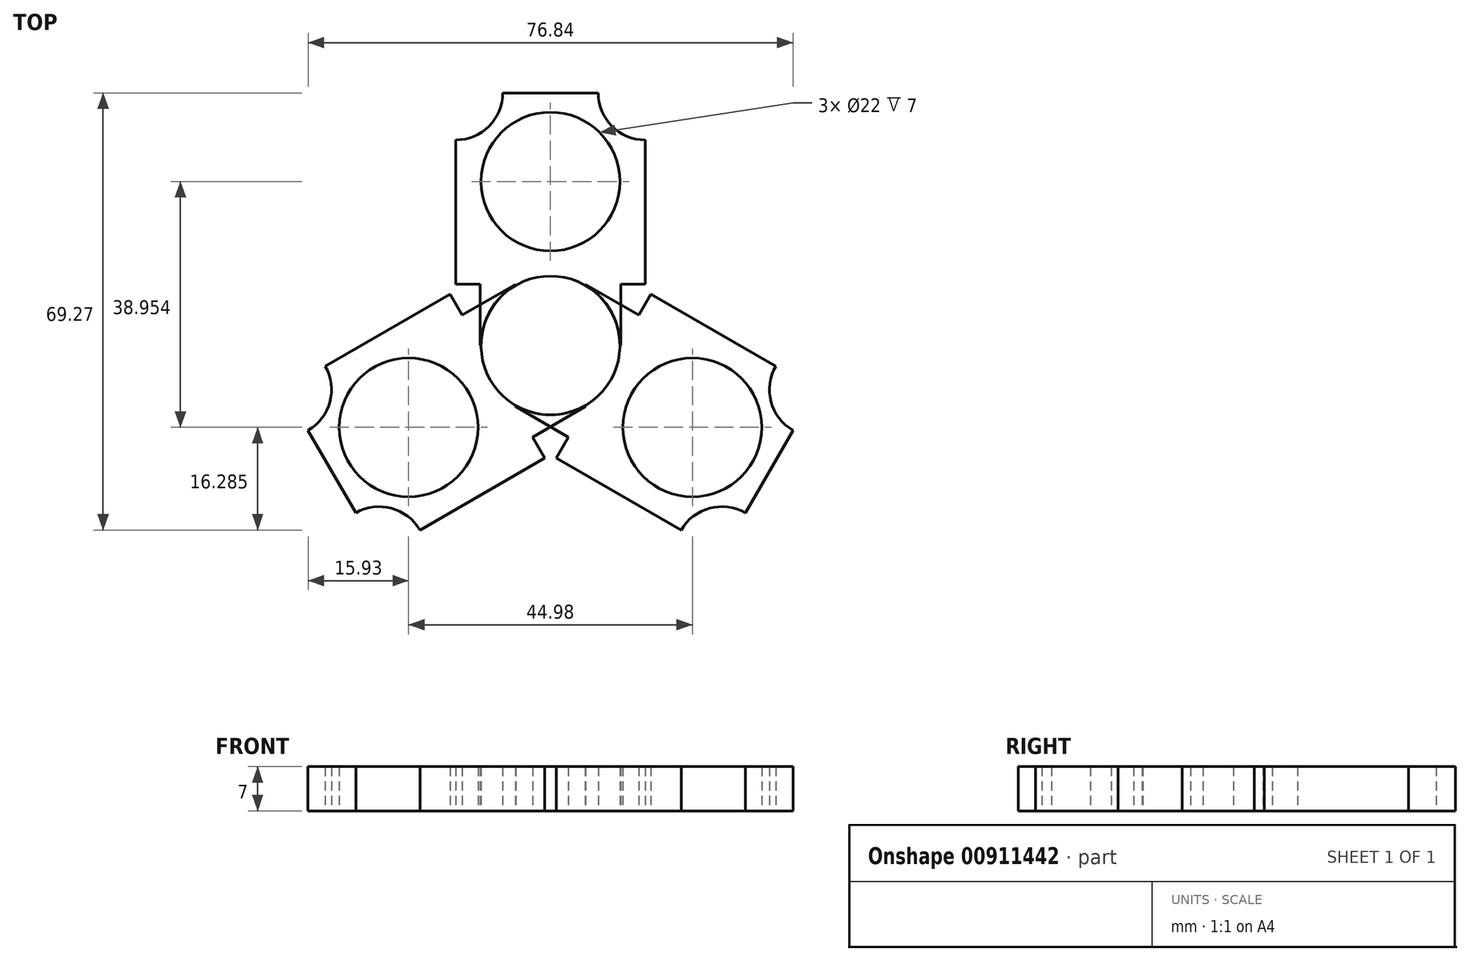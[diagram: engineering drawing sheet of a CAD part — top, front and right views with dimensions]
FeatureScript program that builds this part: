
annotation { "Feature Type Name" : "Feature", "Feature Type Description" : "" }
export const myFeature = defineFeature(function(context is Context, id is Id, definition is map)
    precondition{}
    {
        {
            var Q0;
            Q0=qCreatedBy(makeId("Top.planeOp"),FACE);
            var sketch = newSketch(context, id + "F0", { "sketchPlane" : qUnion([Q0])});
            skCircle(sketch, "E0", {"center": v(0, 0) * mm, "radius": 11 * mm});
            skLineSegment(sketch, "E1.bottom", {"start": v(0, 0) * mm, "end": v(15, 0) * mm});
            skLineSegment(sketch, "E1.top", {"start": v(0, 40) * mm, "end": v(15, 40) * mm});
            skLineSegment(sketch, "E1.left", {"start": v(0, 0) * mm, "end": v(0, 40) * mm});
            skLineSegment(sketch, "E1.right", {"start": v(15, 0) * mm, "end": v(15, 40) * mm});
            skLineSegment(sketch, "E2.bottom", {"start": v(0, 0) * mm, "end": v(-15, 0) * mm});
            skLineSegment(sketch, "E2.top", {"start": v(0, 40) * mm, "end": v(-15, 40) * mm});
            skLineSegment(sketch, "E2.right", {"start": v(-15, 0) * mm, "end": v(-15, 40) * mm});
            skLineSegment(sketch, "E3", {"start": v(0, 40) * mm, "end": v(0, 25.97) * mm});
            skCircle(sketch, "E4", {"center": v(0, 25.97) * mm, "radius": 11 * mm});
            skCircle(sketch, "E5", {"center": v(15, 40) * mm, "radius": 7.44 * mm});
            skCircle(sketch, "E6", {"center": v(-15, 40) * mm, "radius": 7.44 * mm});
            skLineSegment(sketch, "E7.bottom", {"start": v(-15, 0) * mm, "end": v(-11.16, 0) * mm});
            skLineSegment(sketch, "E7.top", {"start": v(-15, 9.7) * mm, "end": v(-11.16, 9.7) * mm});
            skLineSegment(sketch, "E7.left", {"start": v(-15, 0) * mm, "end": v(-15, 9.7) * mm});
            skLineSegment(sketch, "E7.right", {"start": v(-11.16, 0) * mm, "end": v(-11.16, 9.7) * mm});
            skLineSegment(sketch, "E8.bottom", {"start": v(15, 0) * mm, "end": v(11.16, 0) * mm});
            skLineSegment(sketch, "E8.top", {"start": v(15, 9.7) * mm, "end": v(11.16, 9.7) * mm});
            skLineSegment(sketch, "E8.left", {"start": v(15, 0) * mm, "end": v(15, 9.7) * mm});
            skLineSegment(sketch, "E8.right", {"start": v(11.16, 0) * mm, "end": v(11.16, 9.7) * mm});
            skSolve(sketch);
        }
        {
            var Q0;
            {var subQ1=sQuery(id+"F0.wireOp",EDGE,"E1.bottom");var subQ10=sQuery(id+"F0.wireOp",EDGE,"E0");var subQ11=makeQuery(id+"F0.imprint","INTERSECT",VERTEX,{"derivedFrom":[subQ10,subQ1]});Q0=makeQuery(id+"F0.imprint","IMPRINT",FACE,{"disambiguationData":[TD([[makeQuery(id+"F0.imprint","IMPRINT",EDGE,{"disambiguationData":[TD([[subQ11,-1.0]])],"derivedFrom":subQ10}),-1.0]])]});}
            var Q1;
            {var subQ1=sQuery(id+"F0.wireOp",EDGE,"E0");var subQ10=sQuery(id+"F0.wireOp",EDGE,"E2.bottom");var subQ12=makeQuery(id+"F0.imprint","INTERSECT",VERTEX,{"derivedFrom":[subQ1,subQ10]});Q1=makeQuery(id+"F0.imprint","IMPRINT",FACE,{"disambiguationData":[TD([[makeQuery(id+"F0.imprint","IMPRINT",EDGE,{"disambiguationData":[TD([[subQ12,1.0]])],"derivedFrom":subQ1}),-1.0]])]});}
            extrude(context, id + "F1", {"entities" : qUnion([Q0, Q1]), "depth" : 7 * mm, "offsetDistance" : 25 * mm});
        }
        {
            var Q0;
            Q0=qCreatedBy(makeId("Front.planeOp"),FACE);
            var sketch = newSketch(context, id + "F2", { "sketchPlane" : qUnion([Q0])});
            skLineSegment(sketch, "E9", {"start": v(0, 0) * mm, "end": v(0, 33.84) * mm});
            skSolve(sketch);
        }
        {
            var Q0;
            Q0=makeQuery(id+"F1.opExtrude","SWEPT_BODY",BODY,{"disambiguationData":[OSD([sQuery(id+"F0.wireOp",EDGE,"E0"),sQuery(id+"F0.wireOp",EDGE,"E1.bottom"),sQuery(id+"F0.wireOp",EDGE,"E1.top"),sQuery(id+"F0.wireOp",EDGE,"E1.right"),sQuery(id+"F0.wireOp",EDGE,"E2.bottom"),sQuery(id+"F0.wireOp",EDGE,"E2.top"),sQuery(id+"F0.wireOp",EDGE,"E2.right"),sQuery(id+"F0.wireOp",EDGE,"E4")])]});
            var Q1;
            Q1=sQuery(id+"F2.wireOp",EDGE,"E9");
            transform(context, id + "F3", {"entities" : qUnion([Q0]), "transformType" : TransformType.ROTATION, "transformAxis" : qUnion([Q1]), "angle" : 120 * degree, "makeCopy" : true});
        }
        {
            var Q0;
            Q0=makeQuery(id+"F3.opPattern","COPY",BODY,{"derivedFrom":makeQuery(id+"F1.opExtrude","SWEPT_BODY",BODY,{"disambiguationData":[OSD([sQuery(id+"F0.wireOp",EDGE,"E0"),sQuery(id+"F0.wireOp",EDGE,"E1.bottom"),sQuery(id+"F0.wireOp",EDGE,"E1.top"),sQuery(id+"F0.wireOp",EDGE,"E1.right"),sQuery(id+"F0.wireOp",EDGE,"E2.bottom"),sQuery(id+"F0.wireOp",EDGE,"E2.top"),sQuery(id+"F0.wireOp",EDGE,"E2.right"),sQuery(id+"F0.wireOp",EDGE,"E4")])]}),"instanceName":"1"});
            var Q1;
            Q1=sQuery(id+"F2.wireOp",EDGE,"E9");
            transform(context, id + "F4", {"entities" : qUnion([Q0]), "transformType" : TransformType.ROTATION, "transformAxis" : qUnion([Q1]), "angle" : 120 * degree, "makeCopy" : true});
        }
    });
